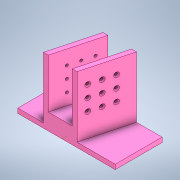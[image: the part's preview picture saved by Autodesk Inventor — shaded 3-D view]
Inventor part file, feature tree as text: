
AUTODESK INVENTOR PART (.ipt)
format: ipt  version: 2022.2 (Build 262287000, 287)  size: 214,016 bytes
history: native  units: mm
features: sketch x5, extrude x3, hole x2
ambient origin geometry x8: Origin, YZ Plane, XZ Plane, XY Plane, X Axis, Y Axis, Z Axis, Center Point
bodies: Body1 (feature_tree)
feature tree (10):
  extrude  "Extrusion8"  Depth=166.0mm
  extrude  "Extrusion11"  TaperAngle=0.0deg  [1 undecoded]
  extrude  "Extrusion12"  Depth=8.0mm
  hole  "HoleForLeftSideOf2x4"  [1 undecoded]
  hole  "HolesForRightSideOf2x4"  [1 undecoded]
  sketch  "Sketch8"  dims[d28=80.0mm d29=166.0mm]
  sketch  "Sketch11"  dims[d30=8.0mm d31=0.0mm]
  sketch  "Sketch12"  dims[d39=-2.617994mm d40=8.0mm]
  sketch  "Sketch15"  dims[d42=8.0mm d44=20.32mm]
  sketch  "Sketch16"  dims[d45=20.32mm d46=104.1375mm d47=0.0mm d49=20.0mm d50=0.0mm d64=15.0mm d65=4.496mm d66=6.0mm d67=8.433mm d68=2.794mm d69=14.3117mm d70=8.0mm d71=0.0mm d72=30.0mm d74=20.0mm d75=30.0mm d77=20.0mm d80=20.0mm d81=15.0mm d82=30.0mm d84=20.0mm d85=30.0mm d87=20.0mm d90=20.0mm d91=4.496mm d92=6.0mm d93=8.433mm d94=2.0mm d95=14.3117mm d96=8.0mm d97=0.0mm d73=0.0625mm]
note: 3 required parameter values undecoded (feature->parameter linkage not recoverable at this tier; creation-order binding heuristic only, values carry confidence <= 0.55)
